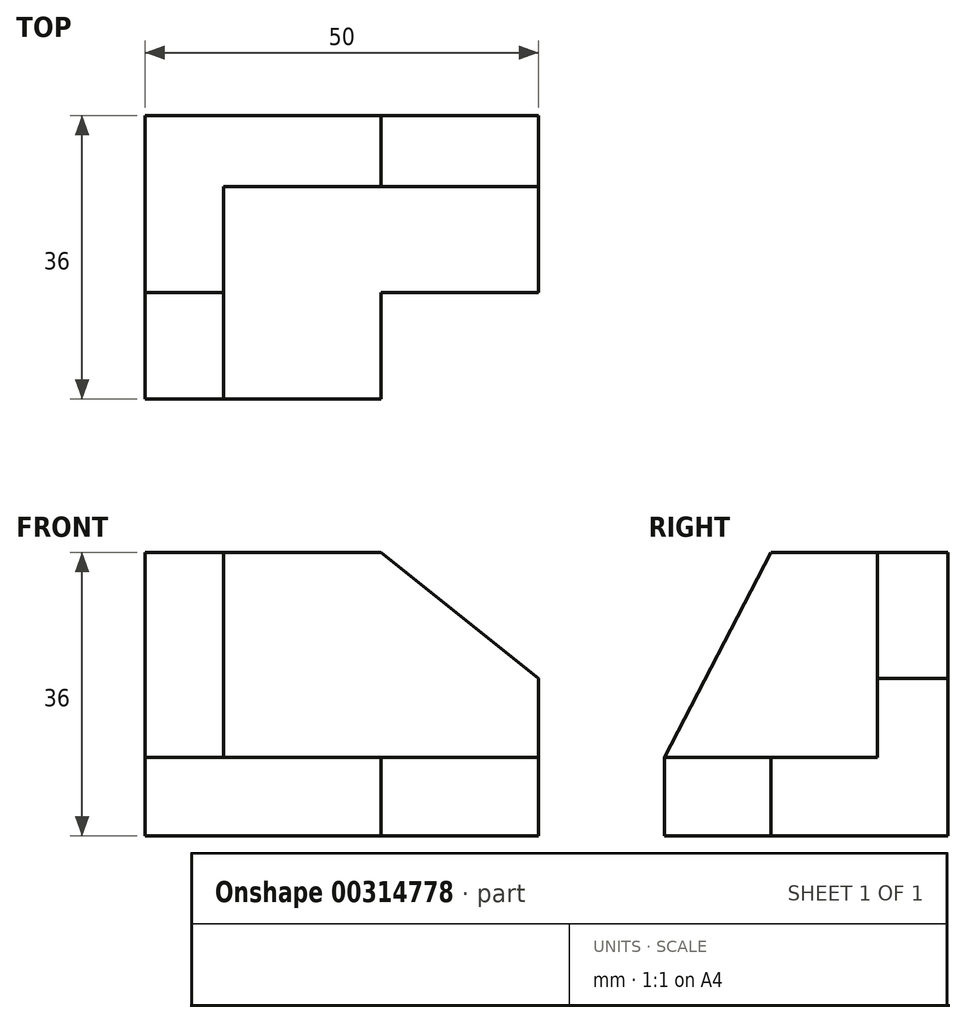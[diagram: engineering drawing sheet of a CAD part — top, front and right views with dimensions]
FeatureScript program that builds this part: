
annotation { "Feature Type Name" : "Feature", "Feature Type Description" : "" }
export const myFeature = defineFeature(function(context is Context, id is Id, definition is map)
    precondition{}
    {
        {
            var Q0;
            Q0=qCreatedBy(makeId("Front.planeOp"),FACE);
            var sketch = newSketch(context, id + "F0", { "sketchPlane" : qUnion([Q0])});
            skLineSegment(sketch, "E0.bottom", {"start": v(0, 0) * mm, "end": v(50, 0) * mm});
            skLineSegment(sketch, "E0.top", {"start": v(0, 36) * mm, "end": v(50, 36) * mm});
            skLineSegment(sketch, "E0.left", {"start": v(0, 0) * mm, "end": v(0, 36) * mm});
            skLineSegment(sketch, "E0.right", {"start": v(50, 0) * mm, "end": v(50, 36) * mm});
            skLineSegment(sketch, "E1", {"start": v(30, 36) * mm, "end": v(50, 20) * mm});
            skLineSegment(sketch, "E2.bottom", {"start": v(50, 36) * mm, "end": v(10, 36) * mm});
            skLineSegment(sketch, "E2.top", {"start": v(50, 10) * mm, "end": v(10, 10) * mm});
            skLineSegment(sketch, "E2.left", {"start": v(50, 36) * mm, "end": v(50, 10) * mm});
            skLineSegment(sketch, "E2.right", {"start": v(10, 36) * mm, "end": v(10, 10) * mm});
            skSolve(sketch);
        }
        {
            var Q0;
            {var subQ1=sQuery(id+"F0.wireOp",EDGE,"E0.bottom");Q0=makeQuery(id+"F0.imprint","IMPRINT",FACE,{"disambiguationData":[TD([[makeQuery(id+"F0.imprint","IMPRINT",EDGE,{"derivedFrom":subQ1}),1.0]])]});}
            var Q1;
            {var subQ1=sQuery(id+"F0.wireOp",EDGE,"E1");Q1=makeQuery(id+"F0.imprint","IMPRINT",FACE,{"disambiguationData":[TD([[makeQuery(id+"F0.imprint","IMPRINT",EDGE,{"derivedFrom":subQ1}),-1.0]])]});}
            extrude(context, id + "F1", {"entities" : qUnion([Q0, Q1]), "oppositeDirection" : true, "depth" : 36 * mm});
        }
        {
            var Q0;
            {var subQ1=sQuery(id+"F0.wireOp",EDGE,"E1");Q0=makeQuery(id+"F0.imprint","IMPRINT",FACE,{"disambiguationData":[TD([[makeQuery(id+"F0.imprint","IMPRINT",EDGE,{"derivedFrom":subQ1}),-1.0]])]});}
            extrude(context, id + "F2", {"entities" : qUnion([Q0]), "operationType" : NewBodyOperationType.REMOVE, "oppositeDirection" : true, "depth" : 27 * mm});
        }
        {
            var Q0;
            Q0=makeQuery(id+"F2.boolean.opBoolean","COPY",FACE,{"derivedFrom":makeQuery(id+"F2.opExtrude","SWEPT_FACE",FACE,{"disambiguationData":[OSD([sQuery(id+"F0.wireOp",EDGE,"E2.right")])]})});
            var sketch = newSketch(context, id + "F3", { "sketchPlane" : qUnion([Q0])});
            skLineSegment(sketch, "E3", {"start": v(13.5, 36) * mm, "end": v(0, 10) * mm});
            skSolve(sketch);
        }
        {
            var Q0;
            Q0 = qSketchRegion(id + "F3", true);
            var Q1;
            {var subQ0=sQuery(id+"F3.wireOp",EDGE,"E3");Q1=makeQuery(id+"F3.imprint","IMPRINT",FACE,{"disambiguationData":[TD([[makeQuery(id+"F3.imprint","IMPRINT",EDGE,{"derivedFrom":subQ0}),-1.0]])]});}
            extrude(context, id + "F4", {"entities" : qUnion([Q0, Q1]), "operationType" : NewBodyOperationType.REMOVE, "endBound" : BoundingType.THROUGH_ALL, "oppositeDirection" : true, "depth" : 25 * mm});
        }
        {
            var Q0;
            Q0=makeQuery(id+"F2.boolean.opBoolean","COPY",FACE,{"derivedFrom":makeQuery(id+"F2.opExtrude","SWEPT_FACE",FACE,{"disambiguationData":[OSD([sQuery(id+"F0.wireOp",EDGE,"E2.top")])]})});
            var sketch = newSketch(context, id + "F5", { "sketchPlane" : qUnion([Q0])});
            skPoint(sketch, "E4.oppositeSnap0", {"position": v(10, 13.5) * mm});
            skPoint(sketch, "E4.oppositeSnap1", {"position": v(30, 27) * mm});
            skLineSegment(sketch, "E4.bottom", {"start": v(50, 0) * mm, "end": v(30, 0) * mm});
            skLineSegment(sketch, "E4.top", {"start": v(50, 13.5) * mm, "end": v(30, 13.5) * mm});
            skLineSegment(sketch, "E4.left", {"start": v(50, 0) * mm, "end": v(50, 13.5) * mm});
            skLineSegment(sketch, "E4.right", {"start": v(30, 0) * mm, "end": v(30, 13.5) * mm});
            skSolve(sketch);
        }
        {
            var Q0;
            Q0 = qSketchRegion(id + "F5", true);
            extrude(context, id + "F6", {"entities" : qUnion([Q0]), "operationType" : NewBodyOperationType.REMOVE, "endBound" : BoundingType.THROUGH_ALL, "oppositeDirection" : true, "depth" : 25 * mm});
        }
    });
